# Revit family: Plumbing Fixture-Grease_Interseptor_Mifab_MI-OS
name_source: partatom
category: Plumbing Fixtures
revit_build: Autodesk Revit Structure 2013 (Build: 20120221_2030(x64)
units: mm (PartAtom-declared; Revit-internal decimal feet)

## types (5) — shared parameters
Assembly Code = D2090300
Description = Oil / Sediment Interceptor
Interceptor Material = Acid Resistant Epoxy Coated Green
Manufacturer = MIFAB
URL = www.mifab.com
zero-valued in all types: Default Elevation, WFU

## per-type parameters (varying)
| type | A | B | C | D | E | F | Sludge Capacity | Standard Inlet And Outlet Radii | Water Capacity |
| MI-OS-1 | 24.375 " | 12.5 " | 4.5 " | 10.5 " | 15 " | 2 " | 12 lbs | 1 " | 12 Gallons |
| MI-OS-2 | 24.375 " | 24.5 " | 7.625 " | 17.625 " | 25.25 " | 4 " | 60 lbs | 2 " | 40 Gallons |
| MI-OS-3 | 36.625 " | 24.375 " | 11 " | 22 " | 33 " | 4 " | 100 lbs | 2 " | 77 Gallons |
| MI-OS-4 | 48.75 " | 24.375 " | 11 " | 22 " | 33 " | 4 " | 200 lbs | 2 " | 103 Gallons |
| MI-OS-5 | 48.75 " | 48.675 " | 11 " | 22 " | 33 " | 4 " | 300 lbs | 2 " | 193.33 Gallons |

note: column(s) folded — value = type name in every type: Model

## geometry (parser evidence)
native form markers: Blend x4, Sweep x1
no freeform markers — native parametric forms only
